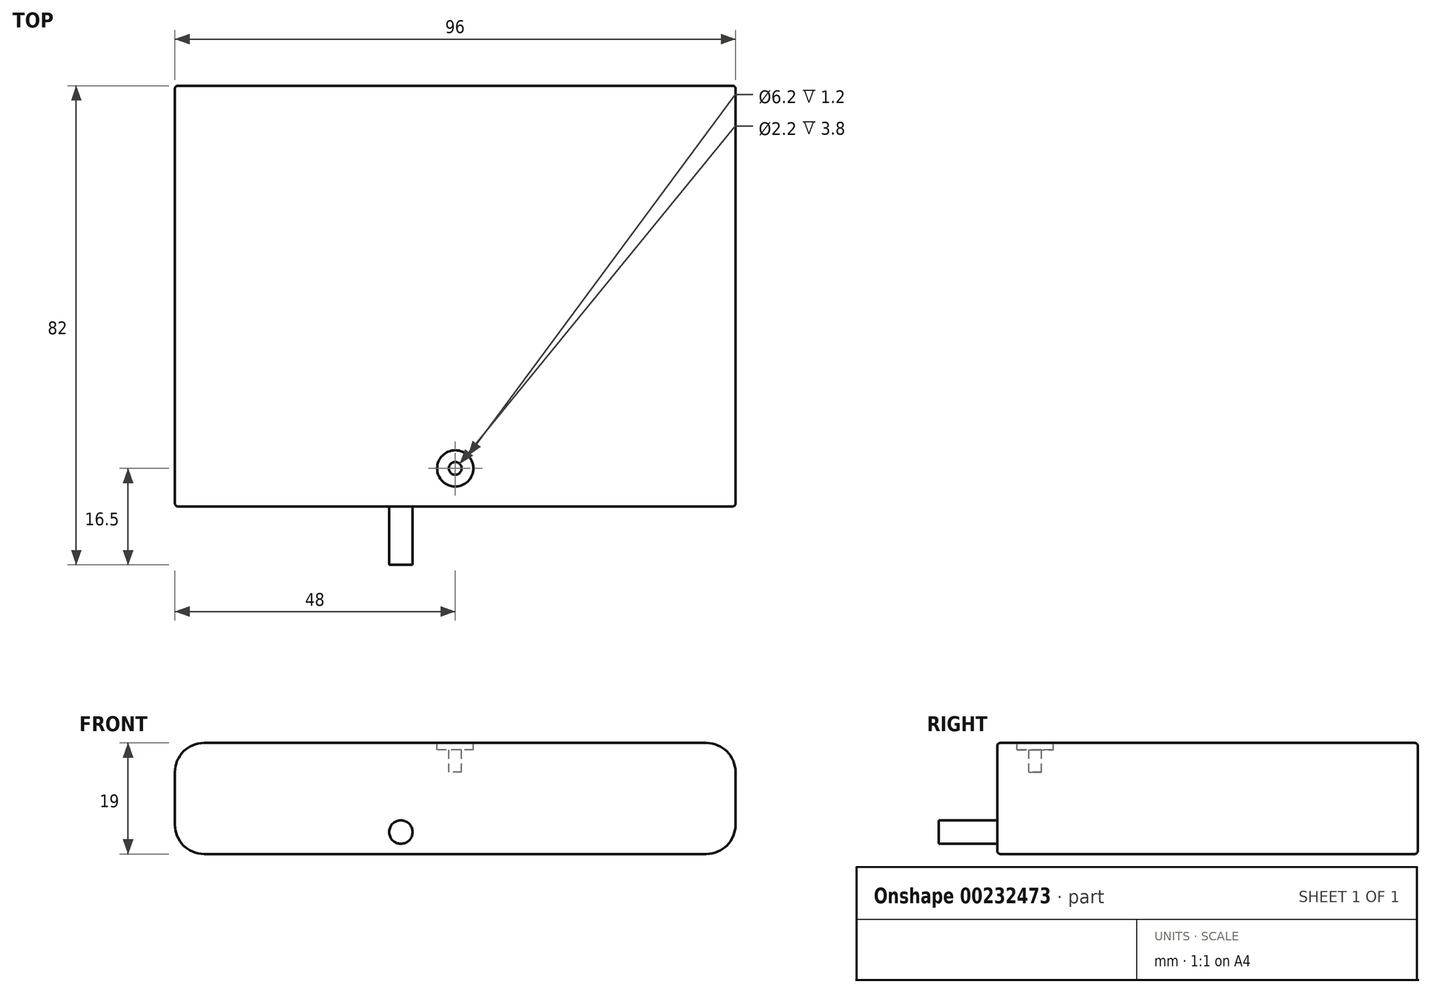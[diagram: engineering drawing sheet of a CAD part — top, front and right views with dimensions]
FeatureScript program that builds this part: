
annotation { "Feature Type Name" : "Feature", "Feature Type Description" : "" }
export const myFeature = defineFeature(function(context is Context, id is Id, definition is map)
    precondition{}
    {
        {
            var Q0;
            Q0=qCreatedBy(makeId("Top.planeOp"),FACE);
            var sketch = newSketch(context, id + "F0", { "sketchPlane" : qUnion([Q0])});
            skLineSegment(sketch, "E0.bottom", {"start": v(48, 36) * mm, "end": v(-48, 36) * mm});
            skLineSegment(sketch, "E0.top", {"start": v(48, -36) * mm, "end": v(-48, -36) * mm});
            skLineSegment(sketch, "E0.left", {"start": v(48, 36) * mm, "end": v(48, -36) * mm});
            skLineSegment(sketch, "E0.right", {"start": v(-48, 36) * mm, "end": v(-48, -36) * mm});
            skPoint(sketch, "E0.middle", {"position": v(0, 0) * mm});
            skSolve(sketch);
        }
        {
            var Q0;
            Q0 = qSketchRegion(id + "F0", true);
            extrude(context, id + "F1", {"entities" : qUnion([Q0]), "depth" : 19 * mm});
        }
        {
            var Q0;
            Q0=makeQuery(id+"F1.opExtrude","CAP_EDGE",EDGE,{"disambiguationData":[OSD([sQuery(id+"F0.wireOp",EDGE,"E0.left")])],"isStart":false});
            var Q1;
            Q1=makeQuery(id+"F1.opExtrude","CAP_EDGE",EDGE,{"disambiguationData":[OSD([sQuery(id+"F0.wireOp",EDGE,"E0.left")])],"isStart":true});
            var Q2;
            Q2=makeQuery(id+"F1.opExtrude","CAP_EDGE",EDGE,{"disambiguationData":[OSD([sQuery(id+"F0.wireOp",EDGE,"E0.right")])],"isStart":false});
            var Q3;
            Q3=makeQuery(id+"F1.opExtrude","CAP_EDGE",EDGE,{"disambiguationData":[OSD([sQuery(id+"F0.wireOp",EDGE,"E0.right")])],"isStart":true});
            fillet(context, id + "F2", {"entities" : qUnion([Q0, Q1, Q2, Q3]), "radius" : 5 * mm, "tangentPropagation" : true, "allowEdgeOverflow" : false});
        }
        {
            var Q0;
            Q0=makeQuery(id+"F1.opExtrude","SWEPT_FACE",FACE,{"disambiguationData":[OSD([sQuery(id+"F0.wireOp",EDGE,"E0.top")])]});
            var Q1;
            Q1=makeQuery(id+"F1.opExtrude","SWEPT_FACE",FACE,{"disambiguationData":[OSD([sQuery(id+"F0.wireOp",EDGE,"E0.bottom")])]});
            fillet(context, id + "F3", {"entities" : qUnion([Q0, Q1]), "radius" : .5 * mm, "tangentPropagation" : true, "allowEdgeOverflow" : false});
        }
        {
            var Q0;
            Q0=makeQuery(id+"F1.opExtrude","SWEPT_FACE",FACE,{"disambiguationData":[OSD([sQuery(id+"F0.wireOp",EDGE,"E0.top")])]});
            var sketch = newSketch(context, id + "F4", { "sketchPlane" : qUnion([Q0])});
            skCircle(sketch, "E1", {"center": v(-9.3, 3.75) * mm, "radius": 2 * mm});
            skSolve(sketch);
        }
        {
            var Q0;
            Q0 = qSketchRegion(id + "F4", true);
            extrude(context, id + "F5", {"entities" : qUnion([Q0]), "operationType" : NewBodyOperationType.ADD, "depth" : 10 * mm});
        }
        {
            var Q0;
            Q0=makeQuery(id+"F1.opExtrude","CAP_FACE",FACE,{"disambiguationData":[OSD([sQuery(id+"F0.wireOp",EDGE,"E0.bottom"),sQuery(id+"F0.wireOp",EDGE,"E0.top"),sQuery(id+"F0.wireOp",EDGE,"E0.left"),sQuery(id+"F0.wireOp",EDGE,"E0.right")])],"isStart":false});
            var sketch = newSketch(context, id + "F6", { "sketchPlane" : qUnion([Q0])});
            skCircle(sketch, "E2", {"center": v(0, -29.5) * mm, "radius": 3.1 * mm});
            skCircle(sketch, "E3", {"center": v(0, -29.5) * mm, "radius": 1.1 * mm});
            skSolve(sketch);
        }
        {
            var Q0;
            Q0=makeQuery(id+"F6.imprint","IMPRINT",FACE,{"disambiguationData":[TD([[makeQuery(id+"F6.imprint","IMPRINT",EDGE,{"derivedFrom":sQuery(id+"F6.wireOp",EDGE,"E3")}),1.0]])]});
            extrude(context, id + "F7", {"entities" : qUnion([Q0]), "operationType" : NewBodyOperationType.REMOVE, "oppositeDirection" : true, "depth" : 5 * mm});
        }
        {
            var Q0;
            Q0=makeQuery(id+"F6.imprint","IMPRINT",FACE,{"disambiguationData":[TD([[makeQuery(id+"F6.imprint","IMPRINT",EDGE,{"derivedFrom":sQuery(id+"F6.wireOp",EDGE,"E2")}),1.0]])]});
            extrude(context, id + "F8", {"entities" : qUnion([Q0]), "operationType" : NewBodyOperationType.REMOVE, "oppositeDirection" : true, "depth" : 1.2 * mm});
        }
    });
